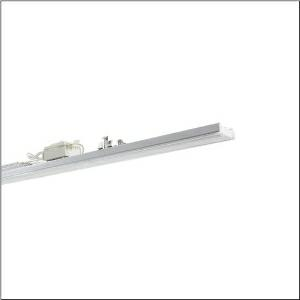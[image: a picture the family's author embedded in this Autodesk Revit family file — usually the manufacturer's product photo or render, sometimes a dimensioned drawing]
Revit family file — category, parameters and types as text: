
# Revit family: licross_r__11_recessed_mo_51te12mn4axg_042f
name_source: partatom
category: Lighting Fixtures
units: mm (PartAtom-declared; Revit-internal decimal feet)

## family parameters
Cut with Voids When Loaded = No
Host = Face
Light Source = No
Part Type = Normal
Room Calculation Point = No
Round Connector Dimension = Use Diameter
Shared = No

## types (1)
- --- (1 x LED, 10290 lm, 55.2 W, 4000K)
    Apparent Load = 55 VA
    CIE Flux Codes = 67 92 99 100 100
    Color Rendering = 80
    Color Temperature = 4000K
    Default Elevation = 1800 mm
    Description = Licross® 11 Recessed MO, luminaire insert, of sheet steel, galvanised, coil coated, white, length: 1.500mm, width: 66mm, height: 67mm, LED rated luminous flux: 10.290lm, light colour: 840, control gear: ON/OFF Multilumen, with plug, 3-pole, with phase selection, mains connection: 220..240V, AC, 50/60Hz, rated input power: 55W, halogen-free wiring, primary optical cover: cover, of PMMA, light emission: direct distribution, primary light characteristic: symmetric, protection rating (complete): IP54, insulation class (complete): insulation class I (protective earthing), certification: CE, ENEC, VDE, UKCA, protection symbol: D if used in an environment with non-conductive dust loads with corresponding accessories, impact resistance: IK06, permissible ambient temperature for indoor applications: -35..+40°C, corresponds to IFS (International Featured Standards) requirements for safety and quality in the food industry, reducing of maximum allowable ambient temperature of 5°C with ceiling mounting, packaging unit: 1 piece
    Height = 58 mm
    Lamp = 1 x LED
    Lamp Light Flux = 10290 lm
    Lamp Power = 55.2 W
    Lamp count = 1
    Length = 1500 mm
    Luminous efficacy = 186 lm/W
    Manufacturer = Siteco
    ModVariant = No
    Model = 51TE12MN4AXG
    Mounting Place = Ceiling
    Mounting Type = Pendant
    Number of Poles = 1
    OnlyDefault = Yes
    Power Factor = 1
    Product Name = Licross® 11 Recessed MO
    Product group = luminaire insert
    ProductGroupID = 902
    Protection Class = Protection class I
    Protection Degree = IP 54
    RLX_Detail_Level = 1
    RLX_Emergency_Light_Flux = 0 lm
    RLX_Emergency_Type = 0
    RLX_Emergency_Type_DB = No
    RlxData = <blob elided: 22105 chars, md5=603dfbcb>
    Socket = socket
    Standby Power = 0 W
    System Light Flux = 10290 lm
    System Power = 55 W
    Type Comments = factory setting: luminous flux: 100 % | (A | C | E) | 126 mA
    Type Image = l_1296930.jpg
    URL = http://relux.com
    VarID = @adj_085572
    Voltage = 0 V
    Weight = 0.00 kg
    Width = 66 mm

## geometry (parser evidence)
native form markers: Blend x4, Sweep x13
no freeform markers — native parametric forms only
